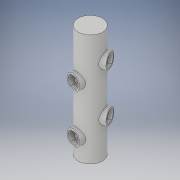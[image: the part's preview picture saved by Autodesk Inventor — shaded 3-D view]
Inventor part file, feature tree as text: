
AUTODESK INVENTOR PART (.ipt)
format: ipt  version: 2017 (Build 210142000, 142)  size: 1,837,568 bytes
history: native  units: in
note: dims shown in document units (in); Inventor stores cm internally (conversion verified against a paired STEP export)
features: extrude x25, sketch x17, other x17, loft x6, shell x1, plane x1, delete_face x1
ambient origin geometry x8: Origin, YZ Plane, XZ Plane, XY Plane, X Axis, Y Axis, Z Axis, Center Point
bodies: Body1 (feature_tree), Body2 (feature_tree), Body3 (feature_tree)
feature tree (68):
  shell  "shell and ramp"  Thickness=15.0in
  extrude  "outer cassing"  Depth=72.0in TaperAngle=0.0deg
  extrude  "bottom"  Depth=3.5in
  sketch  "Sketch2"  dims[d40=1.0in d41=0.0in d44=3.5in]
  other  "Work Axis1"
  other  "ramp"
  other  "ramp light"
  other  "top floor fill workplane"
  extrude  "top floor fill"  Depth=0.5in
  sketch  "Sketch5"  dims[d55=3.0in]
  other  "railing complete"
  other  "light ramp to complete"
  extrude  "top cap"  Depth=9.0in
  plane  "workplane sketch"
  other  "connection plane 1"
  other  "connection plane 2"
  other  "connection workplane 3"
  sketch  "Sketch19"  dims[d64=8.0in d65=1.0in d66=3.1201in d67=0.0in d68=90.0deg d69=90.0deg d70=0.0in d71=0.0in d146=9.0in]
  extrude  "bottom connection"  TaperAngle=90.0deg  [1 undecoded]
  extrude  "bottom connect to case"  TaperAngle=90.0deg  [1 undecoded]
  extrude  "connection cut"  Depth=1.0in TaperAngle=0.0deg
  sketch  "Sketch20"  dims[d147=1.1811in d149=360.0deg d151=90.0deg]
  extrude  "connetion 2"  Depth=9.48in
  extrude  "connection to case 2"  Depth=1.0in TaperAngle=0.0deg
  extrude  "connection cut 2"  Depth=6.6667in TaperAngle=0.0deg
  loft  "connection ramp 2"
  sketch  "Sketch22"  dims[d152=90.0deg d153=90.0deg]
  extrude  "connection 3"  Depth=30.81in
  extrude  "connection to case 3"  Depth=1.0in TaperAngle=0.0deg
  extrude  "connection cut 3"  Depth=41.48in
  loft  "connetion ramp 3"
  sketch  "Sketch23"  dims[d154=6.6667in d157=4.8944in d158=1.0in d159=0.0in d160=1.0in d161=0.0in]
  extrude  "connection 4"  Depth=52.15in
  extrude  "connection to case 4"  Depth=6.6667in TaperAngle=0.0deg
  extrude  "connection cut 4"  Depth=1.0in TaperAngle=0.0deg
  loft  "connection ramp 4"
  sketch  "Sketch24"  dims[d162=2.6875in d163=0.0in d164=9.48in]
  extrude  "connection 5"  Depth=6.6667in
  extrude  "connection to case 5"  Depth=62.8in
  extrude  "connection cut 5"  Depth=1.0in TaperAngle=0.0deg
  loft  "connection ramp 5"
  sketch  "Sketch25"  dims[d165=6.6667in d168=4.8944in d169=1.0in d170=0.0in d171=1.0in d172=0.0in]
  extrude  "connection 6"  TaperAngle=0.0deg  [1 undecoded]
  extrude  "connection to case 6"  Depth=1.0in TaperAngle=0.0deg
  extrude  "connection cut 6"  Depth=1.0in TaperAngle=0.0deg
  loft  "connection ramp 6"
  sketch  "Sketch26"  dims[d173=2.625in d174=0.0in d178=6.6667in d181=4.8944in d182=1.0in d183=0.0in]
  extrude  "connection 7"  Depth=0.5833in
  extrude  "connection to case 7"  Depth=2.0in
  extrude  "connection cut 7"  TaperAngle=90.0deg  [1 undecoded]
  loft  "connection ramp 7"
  delete_face  "Delete Face1"
  sketch  "Sketch1"  dims[d1=16.0in d2=72.0in d3=0.0in]
  sketch  "Sketch4"  dims[d53=3.0in d54=0.5in]
  sketch  "Sketch27"  dims[d184=1.0in d185=0.0in d186=1.0in d187=0.0in]
  sketch  "Sketch28"  dims[d188=20.15in d189=30.81in]
  other  "light railing"
  other  "light railing complete"
  sketch  "Sketch29"  dims[d190=6.6667in d193=4.8944in d194=1.0in d195=0.0in d196=1.0in d197=0.0in]
  sketch  "Sketch30"  dims[d198=1.0in d199=0.0in d200=41.48in]
  other  "Edges2"
  sketch  "Sketch32"  dims[d201=6.6667in d204=4.8944in d205=1.0in d206=0.0in d207=1.0in d208=0.0in]
  other  "Edges4"
  sketch  "Sketch33"  dims[d209=1.0in d210=0.0in d211=52.15in d213=6.6667in d216=4.8944in d217=1.0in d218=0.0in d219=1.0in d220=0.0in d221=1.0in d222=0.0in d228=6.6667in d231=4.8944in d232=62.8in d233=1.0in d234=0.0in d237=1.0in d238=0.0in d239=0.0in d240=1.0in d241=0.0in d242=1.0in d243=0.0in d244=1.0in d245=0.0in d253=0.5833in d254=0.0625in d255=0.0625in d256=0.125in d257=2.0in d268=0.25in d269=0.125in d270=45.0deg d271=0.0892in d272=0.0884in d273=8.0in d274=1.0in d275=3.1201in d276=0.0in d277=90.0deg d278=90.0deg d279=0.0in d280=0.0in d308=3.0in d309=0.5in d310=3.0in d311=0.5833in d312=0.0625in d313=0.0625in d315=0.25in d316=0.125in d317=45.0deg d318=0.0892in d319=0.0884in d320=0.125in d321=90.0deg d322=90.0deg d323=0.0in d324=90.0deg d325=0.0in d326=90.0deg d327=1.0in d329=1.0in d330=0.0in d331=90.0deg d332=0.0in d333=90.0deg d335=1.0in d336=0.0in d337=90.0deg d338=0.0in d339=90.0deg d340=1.0in d341=0.0in d342=90.0deg d343=0.0in d344=90.0deg d346=1.0in d347=0.0in d348=90.0deg d349=0.0in d350=90.0deg d353=1.0in d354=0.0in d355=90.0deg d356=0.0in d357=90.0deg d448=4.0in d449=0.5833in d450=3.8873in d451=3.8873in d452=1.7083in d453=0.0625in d454=0.0625in d455=1.6458in d456=0.25in d457=0.125in d458=0.0884in d459=45.0deg d460=3.3333in d461=0.125in d462=1.0in d477=4.0in d478=0.5833in d479=3.8873in d480=3.8873in d481=1.7083in d482=0.0625in d483=0.0625in d484=1.6458in d485=0.25in d486=0.125in d487=0.0884in d488=45.0deg d489=3.3333in d490=0.125in d491=1.0in d492=4.0in d493=0.5833in d494=3.8873in d495=3.8873in d496=1.7083in d497=0.0625in d498=0.0625in d499=1.6458in d500=0.25in d501=0.125in d502=0.0884in d503=45.0deg d504=3.3333in d505=0.125in d506=1.0in d507=4.0in d508=0.5833in d509=3.8873in d510=3.8873in d511=1.7083in d512=0.0625in d513=0.0625in d514=1.6458in d515=0.25in d516=0.125in d517=0.0884in d518=45.0deg d519=3.3333in d520=0.125in d521=1.0in d522=4.0in d523=0.5833in d524=3.8873in d525=3.8873in d526=1.7083in d527=0.0625in d528=0.0625in d529=1.6458in d530=0.25in d531=0.125in d532=0.0884in d533=45.0deg d534=3.3333in d535=0.125in d536=1.0in d537=4.0in d538=0.5833in d539=3.8873in d540=3.8873in d541=1.7083in d542=0.0625in d543=0.0625in d544=1.6458in d545=0.25in d546=0.125in d547=0.0884in d548=45.0deg d549=3.3333in d550=0.125in d551=1.0in d552=4.0in d553=0.5833in d554=3.8873in d555=3.8873in d556=1.7083in d557=0.0625in d558=0.0625in d559=1.6458in d560=0.25in d561=0.125in d562=0.0884in d563=45.0deg d564=3.3333in d565=0.125in d566=1.0in]
  other  "Edges5"
  other  "Edges6"
  other  "Edges1"
  other  "Edges3"
note: 4 required parameter values undecoded (feature->parameter linkage not recoverable at this tier; creation-order binding heuristic only, values carry confidence <= 0.55)
